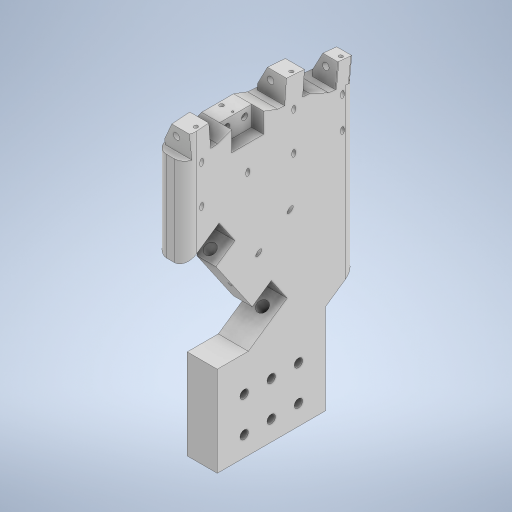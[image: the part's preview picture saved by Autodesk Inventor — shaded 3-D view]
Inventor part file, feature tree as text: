
AUTODESK INVENTOR PART (.ipt)
format: ipt  version: 2024 (Build 280153020, 153B)  size: 570,368 bytes
history: native  units: mm
features: sketch x8, extrude x7, other x6, fillet x2, boolean_combine x1
ambient origin geometry x8: Origin, YZ Plane, XZ Plane, XY Plane, X Axis, Y Axis, Z Axis, Center Point
bodies: Solid1 (feature_tree), Solid2 (feature_tree), Solid3 (feature_tree), Solid4 (feature_tree), Solid5 (feature_tree)
feature tree (24):
  other  "handAssembly.iam"
  other  "palm.ipt:1"
  other  "normMale.ipt:2"
  other  "normMale.ipt:4"
  other  "pinkyMale.ipt:1"
  other  "thumbMale.ipt:1"
  boolean_combine  "Combine1"
  extrude  "Extrusion1"  Depth=10.0mm TaperAngle=0.0deg
  sketch  "Sketch2"  dims[d6=15.0mm d7=0.0mm d8=15.0mm d9=0.0mm]
  extrude  "Extrusion2"  Depth=15.0mm TaperAngle=0.0deg
  extrude  "Extrusion3"  TaperAngle=180.0deg  [1 undecoded]
  extrude  "Extrusion4"  Depth=45.0mm
  extrude  "Extrusion5"  Depth=15.0mm TaperAngle=0.0deg
  fillet  "Fillet4"  Radius=5.5mm
  fillet  "Fillet5"  Radius=5.5mm
  extrude  "Extrusion6"  Depth=4.2mm
  extrude  "Extrusion7"  Depth=10.0mm
  sketch  "Sketch1"  dims[d0=10.0mm d1=34.0mm d2=0.0mm]
  sketch  "Sketch3"  dims[d10=15.509mm d11=180.0deg]
  sketch  "Sketch4"  dims[d12=54.0mm d13=45.0mm]
  sketch  "Sketch5"  dims[d14=15.0mm d15=0.0mm d16=15.0mm d17=0.0mm d18=5.5mm d19=5.5mm]
  sketch  "Sketch6"  dims[d24=4.2mm d25=4.2mm]
  sketch  "Sketch7"  dims[d26=4.2mm d27=10.0mm]
  sketch  "Sketch8"  dims[d28=90.0deg d29=4.2mm d30=4.2mm d31=4.2mm d32=15.0mm d33=0.0mm d34=118.0mm d35=0.0mm d4=0.0mm d5=0.0mm]
note: 1 required parameter value undecoded (feature->parameter linkage not recoverable at this tier; creation-order binding heuristic only, values carry confidence <= 0.55)
